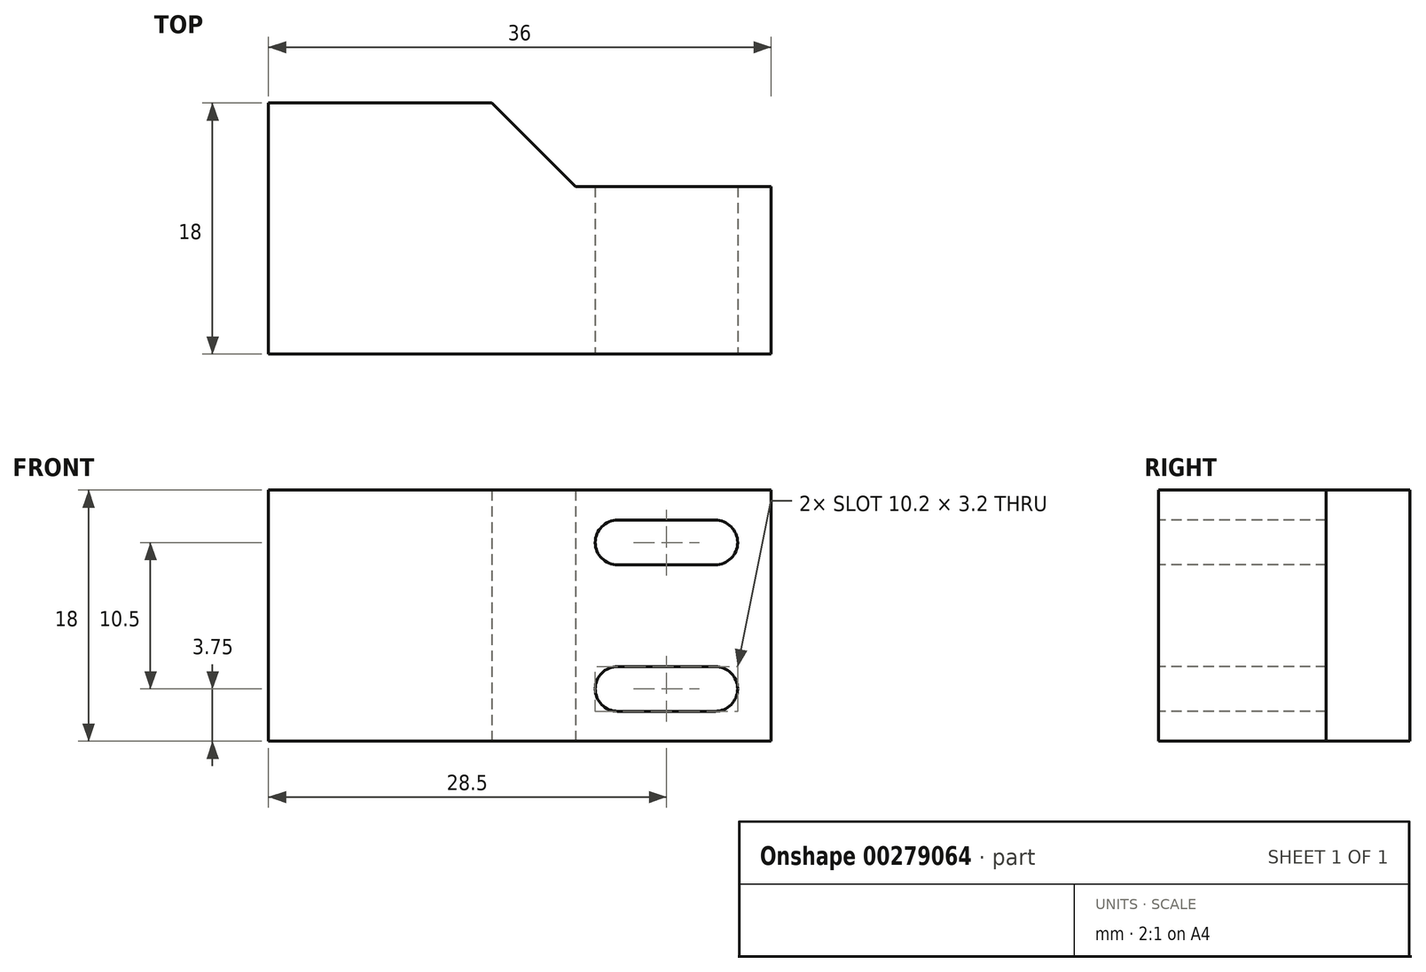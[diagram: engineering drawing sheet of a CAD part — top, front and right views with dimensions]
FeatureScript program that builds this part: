
annotation { "Feature Type Name" : "Feature", "Feature Type Description" : "" }
export const myFeature = defineFeature(function(context is Context, id is Id, definition is map)
    precondition{}
    {
        {
            var Q0;
            Q0=qCreatedBy(makeId("Top.planeOp"),FACE);
            var sketch = newSketch(context, id + "F0", { "sketchPlane" : qUnion([Q0])});
            skLineSegment(sketch, "E0", {"start": v(0, 9) * mm, "end": v(0, -9) * mm});
            skLineSegment(sketch, "E1", {"start": v(0, -9) * mm, "end": v(36, -9) * mm});
            skLineSegment(sketch, "E2", {"start": v(36, -9) * mm, "end": v(36, 3) * mm});
            skLineSegment(sketch, "E3", {"start": v(36, 3) * mm, "end": v(22, 3) * mm});
            skLineSegment(sketch, "E4", {"start": v(22, 3) * mm, "end": v(16, 9) * mm});
            skLineSegment(sketch, "E5", {"start": v(16, 9) * mm, "end": v(0, 9) * mm});
            skSolve(sketch);
        }
        {
            var Q0;
            Q0=makeQuery(id+"F0.imprint","IMPRINT",FACE,{"disambiguationData":[TD([[makeQuery(id+"F0.imprint","IMPRINT",EDGE,{"derivedFrom":sQuery(id+"F0.wireOp",EDGE,"E0")}),1.0]])]});
            extrude(context, id + "F1", {"entities" : qUnion([Q0]), "depth" : 18 * mm, "symmetric" : true});
        }
        {
            var Q0;
            Q0=makeQuery(id+"F1.opExtrude","SWEPT_FACE",FACE,{"disambiguationData":[OSD([sQuery(id+"F0.wireOp",EDGE,"E1")])]});
            var sketch = newSketch(context, id + "F2", { "sketchPlane" : qUnion([Q0])});
            skLineSegment(sketch, "E6", {"start": v(28.5, 9) * mm, "end": v(28.5, -9) * mm, "construction": true});
            skLineSegment(sketch, "E7", {"start": v(32, 5.25) * mm, "end": v(25, 5.25) * mm});
            skArc(sketch, "E8.0.startCap", {"start": v(32, 6.85) * mm, "mid": v(33.6, 5.25) * mm, "end": v(32, 3.65) * mm});
            skArc(sketch, "E8.0.endCap", {"start": v(25, 3.65) * mm, "mid": v(23.4, 5.25) * mm, "end": v(25, 6.85) * mm});
            skLineSegment(sketch, "E8.0.left", {"start": v(32, 3.65) * mm, "end": v(25, 3.65) * mm});
            skLineSegment(sketch, "E8.0.right", {"start": v(32, 6.85) * mm, "end": v(25, 6.85) * mm});
            skLineSegment(sketch, "E9.MirrorCS", {"start": v(32, -6.85) * mm, "end": v(25, -6.85) * mm});
            skArc(sketch, "E10.MirrorCS", {"start": v(25, -3.65) * mm, "mid": v(23.4, -5.25) * mm, "end": v(25, -6.85) * mm});
            skLineSegment(sketch, "E11.MirrorCS", {"start": v(32, -3.65) * mm, "end": v(25, -3.65) * mm});
            skArc(sketch, "E12.MirrorCS", {"start": v(32, -6.85) * mm, "mid": v(33.6, -5.25) * mm, "end": v(32, -3.65) * mm});
            skPoint(sketch, "E13", {"position": v(28.5, 5.25) * mm});
            skSolve(sketch);
        }
        {
            var Q0;
            Q0 = qSketchRegion(id + "F2", true);
            extrude(context, id + "F3", {"entities" : qUnion([Q0]), "operationType" : NewBodyOperationType.REMOVE, "endBound" : BoundingType.THROUGH_ALL, "oppositeDirection" : true, "depth" : 25 * mm});
        }
    });
